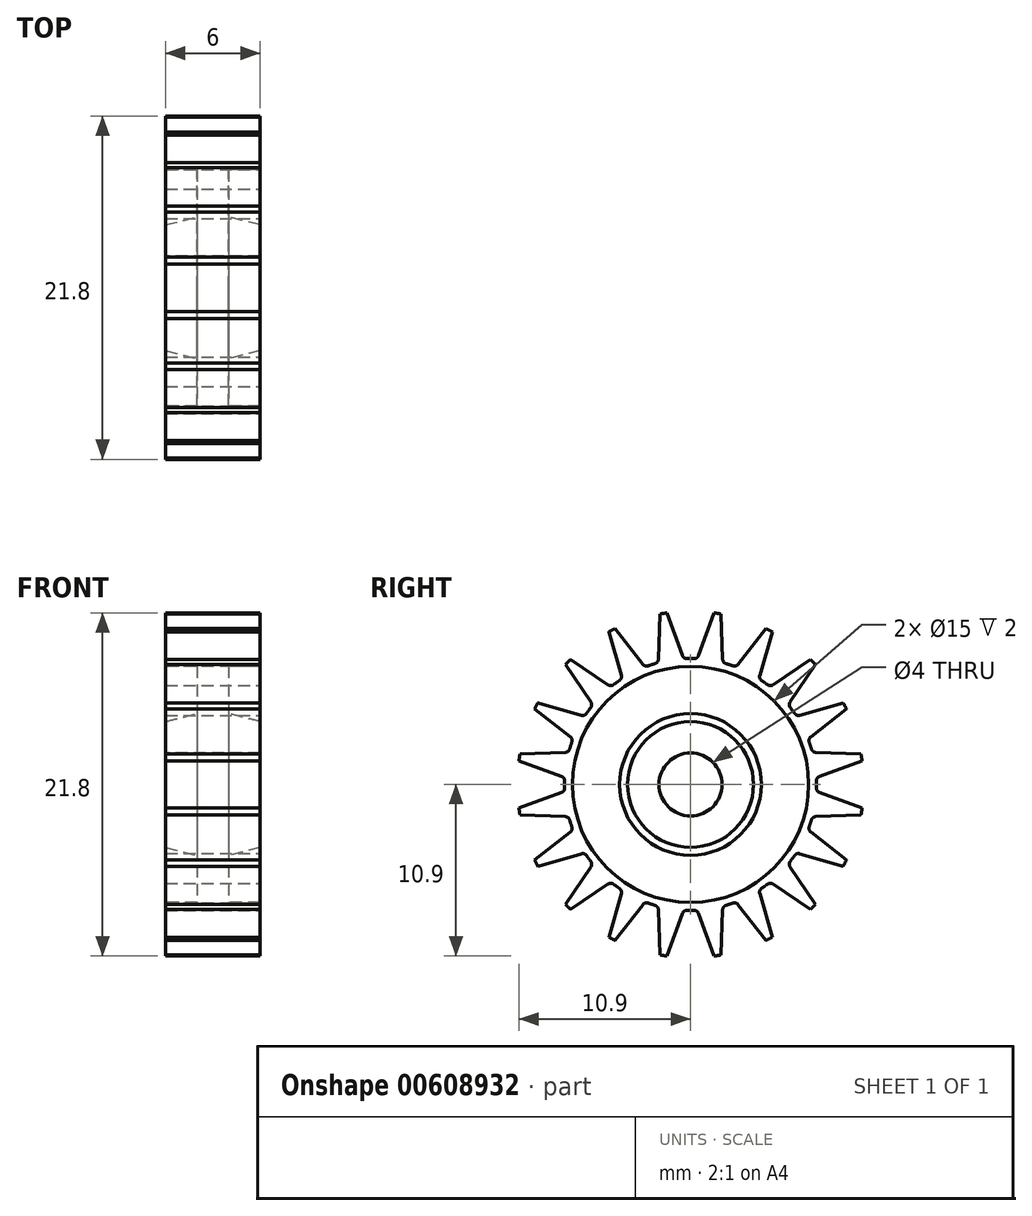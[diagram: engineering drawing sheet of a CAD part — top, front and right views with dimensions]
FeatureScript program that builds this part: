
annotation { "Feature Type Name" : "Feature", "Feature Type Description" : "" }
export const myFeature = defineFeature(function(context is Context, id is Id, definition is map)
    precondition{}
    {
        {
            var Q0;
            Q0=qCreatedBy(makeId("Front.planeOp"),FACE);
            var sketch = newSketch(context, id + "F0", { "sketchPlane" : qUnion([Q0])});
            skLineSegment(sketch, "E0", {"start": v(0, 0) * mm, "end": v(0, 11) * mm, "construction": true});
            skLineSegment(sketch, "E1", {"start": v(0, 11) * mm, "end": v(-3, 11) * mm});
            skLineSegment(sketch, "E2", {"start": v(-3, 11) * mm, "end": v(-3, 7.5) * mm});
            skLineSegment(sketch, "E3", {"start": v(-3, 0) * mm, "end": v(0, 0) * mm, "construction": true});
            skLineSegment(sketch, "E4", {"start": v(-3, 7.5) * mm, "end": v(-1, 7.5) * mm});
            skLineSegment(sketch, "E5", {"start": v(-1, 7.5) * mm, "end": v(-1, 4.5) * mm});
            skLineSegment(sketch, "E6", {"start": v(-3, 2) * mm, "end": v(0, 2) * mm});
            skLineSegment(sketch, "E7", {"start": v(-1, 4.5) * mm, "end": v(-3, 4) * mm});
            skLineSegment(sketch, "E8.trimOffspring", {"start": v(-3, 4) * mm, "end": v(-3, 2) * mm});
            skLineSegment(sketch, "E9.MirrorCS", {"start": v(0, 11) * mm, "end": v(3, 11) * mm});
            skLineSegment(sketch, "E10.MirrorCS", {"start": v(3, 11) * mm, "end": v(3, 7.5) * mm});
            skLineSegment(sketch, "E11.MirrorCS", {"start": v(3, 7.5) * mm, "end": v(1, 7.5) * mm});
            skLineSegment(sketch, "E12.MirrorCS", {"start": v(1, 7.5) * mm, "end": v(1, 4.5) * mm});
            skLineSegment(sketch, "E13.MirrorCS", {"start": v(1, 4.5) * mm, "end": v(3, 4) * mm});
            skLineSegment(sketch, "E14.MirrorCS", {"start": v(3, 4) * mm, "end": v(3, 2) * mm});
            skLineSegment(sketch, "E15.MirrorCS", {"start": v(3, 2) * mm, "end": v(0, 2) * mm});
            skSolve(sketch);
        }
        {
            var Q0;
            Q0=makeQuery(id+"F0.imprint","IMPRINT",FACE,{"disambiguationData":[TD([[makeQuery(id+"F0.imprint","IMPRINT",EDGE,{"derivedFrom":sQuery(id+"F0.wireOp",EDGE,"E1")}),1.0]])]});
            var Q1;
            Q1=sQuery(id+"F0.wireOp",EDGE,"E3");
            revolve(context, id + "F1", {"entities" : qUnion([Q0]), "axis" : qUnion([Q1]), "revolveType" : RevolveType.FULL});
        }
        {
            var Q0;
            Q0=qCreatedBy(makeId("Right.planeOp"),FACE);
            var sketch = newSketch(context, id + "F2", { "sketchPlane" : qUnion([Q0])});
            skLineSegment(sketch, "E16", {"start": v(0, 0) * mm, "end": v(0, 11) * mm, "construction": true});
            skArc(sketch, "E17", {"start": v(0.23, 8) * mm, "mid": v(0, 8) * mm, "end": v(-0.23, 8) * mm});
            skArc(sketch, "E18", {"start": v(1.5, 10.9) * mm, "mid": v(0, 11) * mm, "end": v(-1.5, 10.9) * mm});
            skLineSegment(sketch, "E19", {"start": v(0.52, 8.2) * mm, "end": v(1.5, 10.9) * mm});
            skLineSegment(sketch, "E20.MirrorCS", {"start": v(-0.52, 8.2) * mm, "end": v(-1.5, 10.9) * mm});
            skPoint(sketch, "E21.visualSharp", {"position": v(-0.44, 7.99) * mm});
            skArc(sketch, "E21.filletArc", {"start": v(-0.52, 8.2) * mm, "mid": v(-0.4, 8.05) * mm, "end": v(-0.23, 8) * mm});
            skPoint(sketch, "E22.visualSharp", {"position": v(0.44, 7.99) * mm});
            skArc(sketch, "E22.filletArc", {"start": v(0.23, 8) * mm, "mid": v(0.4, 8.05) * mm, "end": v(0.52, 8.2) * mm});
            skSolve(sketch);
        }
        {
            var Q0;
            Q0 = qSketchRegion(id + "F2", true);
            extrude(context, id + "F3", {"entities" : qUnion([Q0]), "operationType" : NewBodyOperationType.REMOVE, "oppositeDirection" : true, "depth" : 6 * mm, "offsetDistance" : 25 * mm, "symmetric" : true});
        }
        {
            var Q0;
            Q0=makeQuery(id+"F1.opRevolve","SWEPT_BODY",BODY,{"disambiguationData":[OSD([sQuery(id+"F0.wireOp",EDGE,"E1"),sQuery(id+"F0.wireOp",EDGE,"E2"),sQuery(id+"F0.wireOp",EDGE,"E4"),sQuery(id+"F0.wireOp",EDGE,"E5"),sQuery(id+"F0.wireOp",EDGE,"E6"),sQuery(id+"F0.wireOp",EDGE,"E7"),sQuery(id+"F0.wireOp",EDGE,"E8.trimOffspring"),sQuery(id+"F0.wireOp",EDGE,"E9.MirrorCS"),sQuery(id+"F0.wireOp",EDGE,"E10.MirrorCS"),sQuery(id+"F0.wireOp",EDGE,"E11.MirrorCS"),sQuery(id+"F0.wireOp",EDGE,"E12.MirrorCS"),sQuery(id+"F0.wireOp",EDGE,"E13.MirrorCS"),sQuery(id+"F0.wireOp",EDGE,"E14.MirrorCS"),sQuery(id+"F0.wireOp",EDGE,"E15.MirrorCS")])]});
            var Q1;
            Q1=makeQuery(id+"F3.boolean.opBoolean","COPY",FACE,{"derivedFrom":makeQuery(id+"F3.opExtrude","SWEPT_FACE",FACE,{"disambiguationData":[OSD([sQuery(id+"F2.wireOp",EDGE,"E19")])]})});
            var Q2;
            Q2=makeQuery(id+"F3.boolean.opBoolean","COPY",FACE,{"derivedFrom":makeQuery(id+"F3.opExtrude","SWEPT_FACE",FACE,{"disambiguationData":[OSD([sQuery(id+"F2.wireOp",EDGE,"E22.filletArc")])]})});
            var Q3;
            Q3=makeQuery(id+"F3.boolean.opBoolean","COPY",FACE,{"derivedFrom":makeQuery(id+"F3.opExtrude","SWEPT_FACE",FACE,{"disambiguationData":[OSD([sQuery(id+"F2.wireOp",EDGE,"E17")])]})});
            var Q4;
            Q4=makeQuery(id+"F3.boolean.opBoolean","COPY",FACE,{"derivedFrom":makeQuery(id+"F3.opExtrude","SWEPT_FACE",FACE,{"disambiguationData":[OSD([sQuery(id+"F2.wireOp",EDGE,"E21.filletArc")])]})});
            var Q5;
            Q5=makeQuery(id+"F3.boolean.opBoolean","COPY",FACE,{"derivedFrom":makeQuery(id+"F3.opExtrude","SWEPT_FACE",FACE,{"disambiguationData":[OSD([sQuery(id+"F2.wireOp",EDGE,"E20.MirrorCS")])]})});
            var Q6;
            Q6=makeQuery(id+"F1.opRevolve","SWEPT_FACE",FACE,{"disambiguationData":[OSD([sQuery(id+"F0.wireOp",EDGE,"E1"),sQuery(id+"F0.wireOp",EDGE,"E9.MirrorCS")])]});
            circularPattern(context, id + "F4", {"patternType" : PatternType.FACE, "faces" : qUnion([Q1, Q2, Q3, Q4, Q5]), "axis" : qUnion([Q6]), "angle" : 360 * degree, "instanceCount" : 20, "equalSpace" : true});
        }
    });
